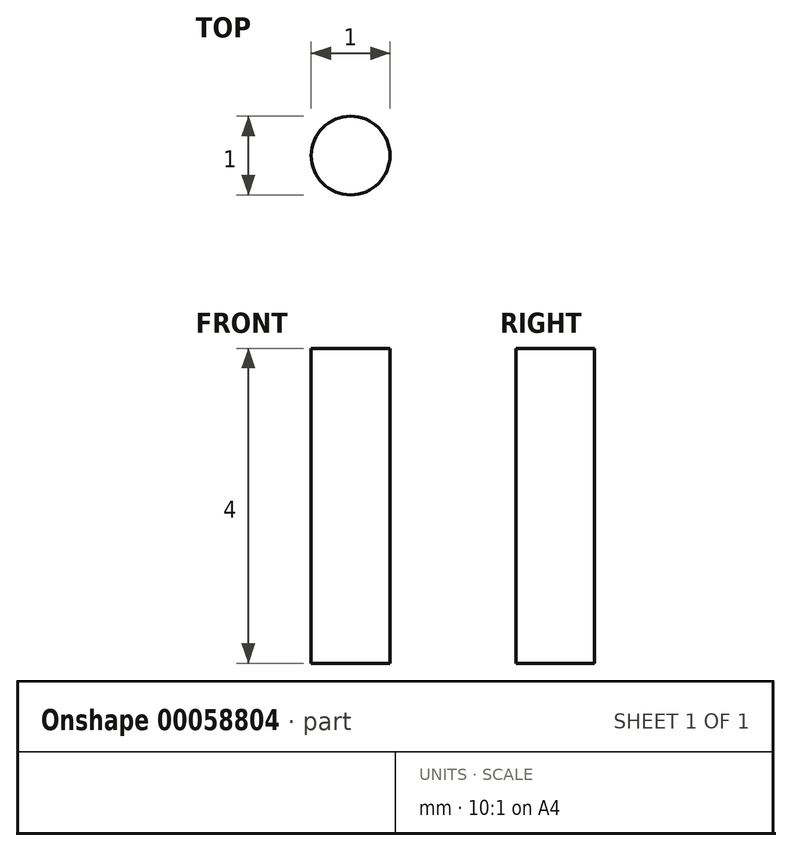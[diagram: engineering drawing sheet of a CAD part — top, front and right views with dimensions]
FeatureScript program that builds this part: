
annotation { "Feature Type Name" : "Feature", "Feature Type Description" : "" }
export const myFeature = defineFeature(function(context is Context, id is Id, definition is map)
    precondition{}
    {
        {
            var Q0;
            Q0=qCreatedBy(makeId("Top.planeOp"),FACE);
            var sketch = newSketch(context, id + "F0", { "sketchPlane" : qUnion([Q0])});
            skCircle(sketch, "E0", {"center": v(0, 0) * mm, "radius": 0.5 * mm});
            skSolve(sketch);
        }
        {
            var Q0;
            Q0 = qSketchRegion(id + "F0", true);
            extrude(context, id + "F1", {"entities" : qUnion([Q0]), "depth" : 4 * mm});
        }
    });
